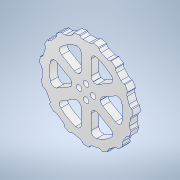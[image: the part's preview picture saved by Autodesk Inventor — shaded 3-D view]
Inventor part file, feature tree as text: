
AUTODESK INVENTOR PART (.ipt)
format: ipt  version: 2022 (Build 260153000, 153)  size: 443,392 bytes
history: native  units: in
note: dims shown in document units (in); Inventor stores cm internally (conversion verified against a paired STEP export)
features: sketch x3, extrude x3, pattern_circular x3, fillet x2, hole x1, other x1
ambient origin geometry x8: Origin, YZ Plane, XZ Plane, XY Plane, X Axis, Y Axis, Z Axis, Center Point
bodies: Body1 (feature_tree)
feature tree (13):
  sketch  "Sketch5"  dims[d20=3.0in d21=0.4528in]
  extrude  "Extrusion4"  Depth=0.4528in
  extrude  "Extrusion5"  TaperAngle=135.0deg  [1 undecoded]
  fillet  "Fillet2"  [1 undecoded]
  pattern_circular  "Circular Pattern2"  [2 undecoded]
  extrude  "Extrusion6"  Depth=0.14in TaperAngle=360.0deg
  fillet  "Fillet1"  Radius=0.2362in
  pattern_circular  "Circular Pattern3"  [2 undecoded]
  hole  "Hole1"  [1 undecoded]
  pattern_circular  "Circular Pattern4"  Count=6 Angle=360.0deg
  sketch  "Sketch6"  dims[d22=0.0787in d23=135.0deg d24=135.0deg]
  sketch  "Sketch7"  dims[d26=0.25in d27=0.0in d28=0.25in d29=0.0in d30=5.9055in d31=360.0deg d34=0.2362in d37=1.0in d38=0.0in d39=0.14in d40=2.3622in d41=360.0deg d43=0.2362in d44=0.177in d45=0.394in d46=0.409in d47=0.25in d48=90.0deg d49=0.559in d50=0.8108in d51=1.5748in d52=360.0deg d57=0.1575in d58=0.1575in d59=60.0deg d60=0.1575in d61=0.315in d62=0.315in d63=0.14in]
  other  "Definition1"
note: 7 required parameter values undecoded (feature->parameter linkage not recoverable at this tier; creation-order binding heuristic only, values carry confidence <= 0.55)
